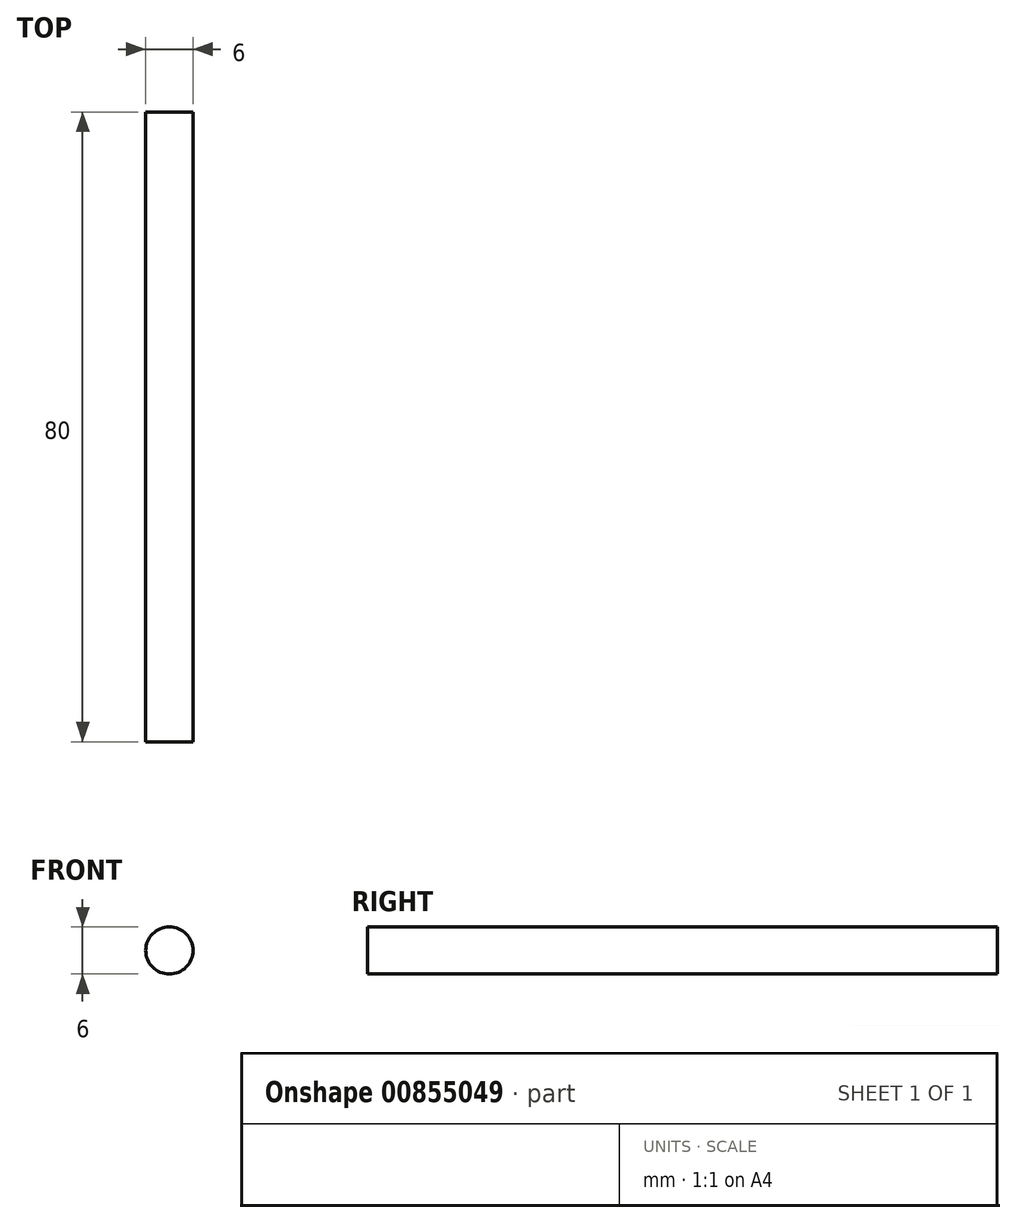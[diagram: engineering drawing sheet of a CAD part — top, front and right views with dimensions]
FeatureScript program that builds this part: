
annotation { "Feature Type Name" : "Feature", "Feature Type Description" : "" }
export const myFeature = defineFeature(function(context is Context, id is Id, definition is map)
    precondition{}
    {
        {
            var Q0;
            Q0=qCreatedBy(makeId("Front.planeOp"),FACE);
            var sketch = newSketch(context, id + "F0", { "sketchPlane" : qUnion([Q0])});
            skCircle(sketch, "E0", {"center": v(0, 0) * mm, "radius": 3 * mm});
            skSolve(sketch);
        }
        {
            var Q0;
            Q0 = qSketchRegion(id + "F0", true);
            extrude(context, id + "F1", {"entities" : qUnion([Q0]), "oppositeDirection" : true, "depth" : 80 * mm, "offsetDistance" : 25 * mm, "symmetric" : true});
        }
    });
